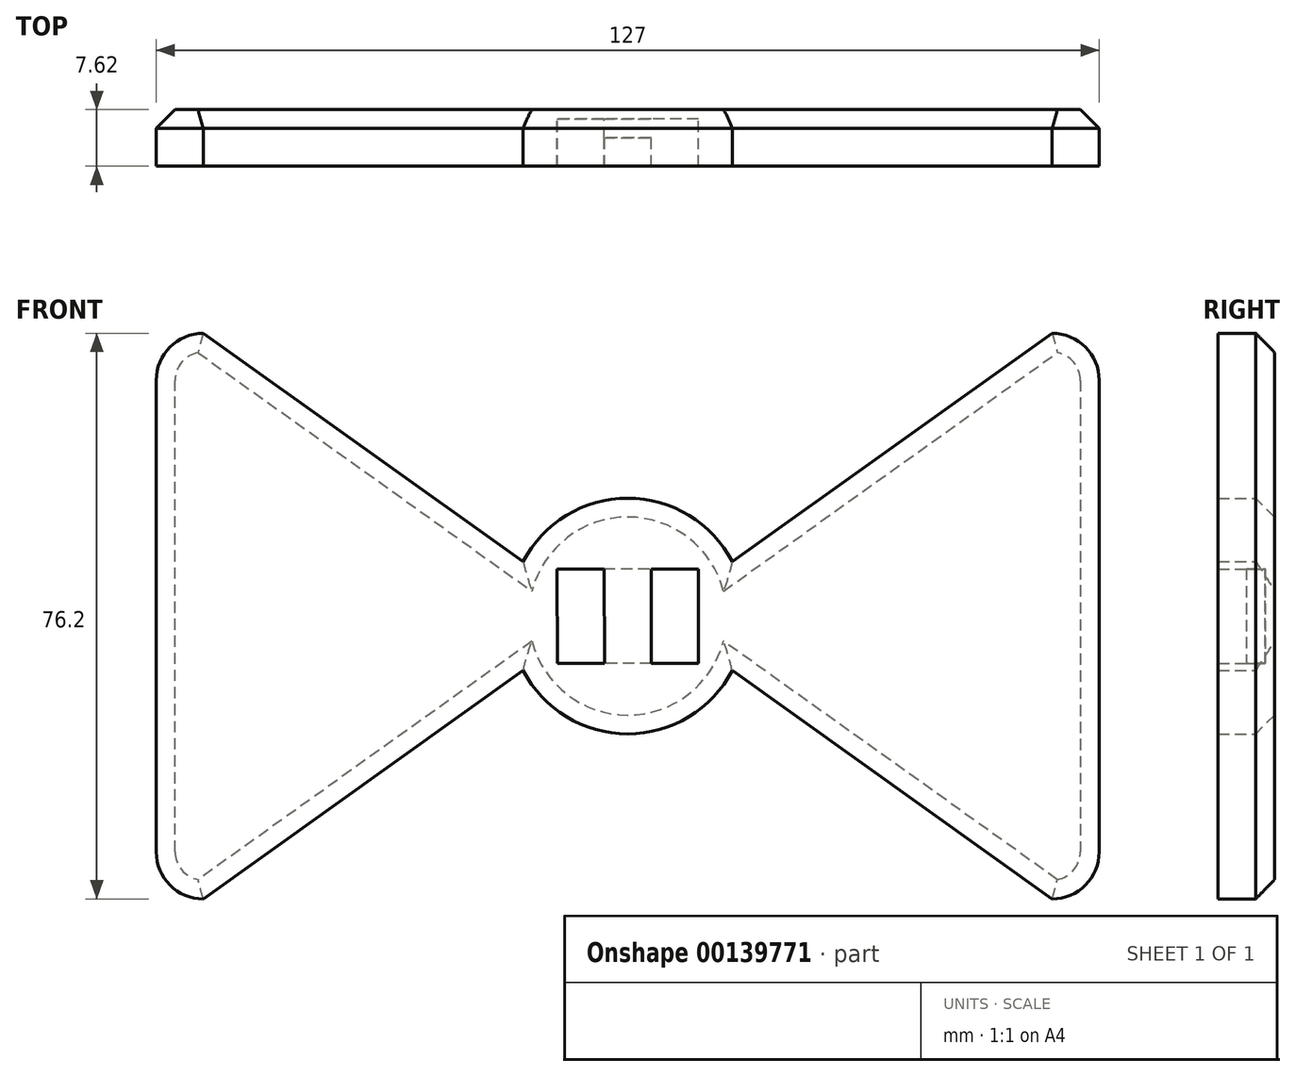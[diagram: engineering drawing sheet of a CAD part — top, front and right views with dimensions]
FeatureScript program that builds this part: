
annotation { "Feature Type Name" : "Feature", "Feature Type Description" : "" }
export const myFeature = defineFeature(function(context is Context, id is Id, definition is map)
    precondition{}
    {
        {
            var Q0;
            Q0=qCreatedBy(makeId("Front.planeOp"),FACE);
            var sketch = newSketch(context, id + "F0", { "sketchPlane" : qUnion([Q0])});
            skPoint(sketch, "E0.middle", {"position": v(0, 0) * mm});
            skPoint(sketch, "E1.endSnap0", {"position": v(12.7, 0) * mm});
            skPoint(sketch, "E2.endSnap0", {"position": v(-12.7, 0) * mm});
            skLineSegment(sketch, "E3", {"start": v(-63.5, 0) * mm, "end": v(-63.5, -31.75) * mm});
            skLineSegment(sketch, "E4", {"start": v(-63.5, 0) * mm, "end": v(-63.5, 31.75) * mm});
            skLineSegment(sketch, "E5", {"start": v(63.5, 0) * mm, "end": v(63.5, -31.75) * mm});
            skLineSegment(sketch, "E6", {"start": v(63.5, 0) * mm, "end": v(63.5, 31.75) * mm});
            skLineSegment(sketch, "E7", {"start": v(-57.15, -38.1) * mm, "end": v(-14.08, -7.33) * mm});
            skLineSegment(sketch, "E8", {"start": v(-57.15, 38.1) * mm, "end": v(-14.08, 7.33) * mm});
            skLineSegment(sketch, "E9", {"start": v(14.08, -7.33) * mm, "end": v(57.15, -38.1) * mm});
            skLineSegment(sketch, "E10", {"start": v(57.15, 38.1) * mm, "end": v(14.08, 7.33) * mm});
            skArc(sketch, "E11", {"start": v(-63.5, 31.75) * mm, "mid": v(-61.64, 36.24) * mm, "end": v(-57.15, 38.1) * mm});
            skArc(sketch, "E12", {"start": v(-63.5, -31.75) * mm, "mid": v(-61.64, -36.24) * mm, "end": v(-57.15, -38.1) * mm});
            skArc(sketch, "E13", {"start": v(63.5, 31.75) * mm, "mid": v(61.64, 36.24) * mm, "end": v(57.15, 38.1) * mm});
            skArc(sketch, "E14", {"start": v(14.08, 7.33) * mm, "mid": v(0, 15.88) * mm, "end": v(-14.08, 7.33) * mm});
            skPoint(sketch, "E15.orphan", {"position": v(-12.7, -12.7) * mm});
            skPoint(sketch, "E16.orphan", {"position": v(12.7, -12.7) * mm});
            skArc(sketch, "E17.trimOffspring", {"start": v(-14.08, -7.33) * mm, "mid": v(0, -15.88) * mm, "end": v(14.08, -7.33) * mm});
            skPoint(sketch, "E18.trimOffspring.end.orphan", {"position": v(-12.7, 12.7) * mm});
            skPoint(sketch, "E19.orphan", {"position": v(12.7, 12.7) * mm});
            skPoint(sketch, "E20.trimOffspring.start.orphan", {"position": v(12.7, 6.35) * mm});
            skArc(sketch, "E21", {"start": v(63.5, -31.75) * mm, "mid": v(61.64, -36.24) * mm, "end": v(57.15, -38.1) * mm});
            skSolve(sketch);
        }
        {
            var Q0;
            Q0=qSketchRegion(id+"F0",true);
            extrude(context, id + "F1", {"entities" : qUnion([Q0]), "depth" : 12.7 * mm});
        }
        {
            var Q0;
            Q0=qSketchRegion(id+"F0",true);
            extrude(context, id + "F2", {"entities" : qUnion([Q0]), "operationType" : NewBodyOperationType.ADD, "depth" : 12.7 * mm});
        }
        {
            var Q0;
            Q0=qCreatedBy(makeId("Front.planeOp"),FACE);
            cPlane(context, id + "F3", {"entities" : qUnion([Q0]), "cplaneType" : CPlaneType.OFFSET, "offset" : 6.35 * mm, "width" : 152.4 * mm, "height" : 152.4 * mm});
        }
        {
            var Q0;
            Q0=qCreatedBy(id+"F3.planeOp",FACE);
            var sketch = newSketch(context, id + "F4", { "sketchPlane" : qUnion([Q0])});
            skLineSegment(sketch, "E22", {"start": v(3.18, 6.35) * mm, "end": v(3.18, -6.35) * mm});
            skLineSegment(sketch, "E23", {"start": v(3.18, -6.35) * mm, "end": v(9.53, -6.35) * mm});
            skLineSegment(sketch, "E24", {"start": v(9.53, -6.35) * mm, "end": v(9.53, 6.35) * mm});
            skLineSegment(sketch, "E25", {"start": v(9.53, 6.35) * mm, "end": v(3.18, 6.35) * mm});
            skLineSegment(sketch, "E26", {"start": v(-3.17, 6.35) * mm, "end": v(-3.11, -6.35) * mm});
            skLineSegment(sketch, "E27", {"start": v(-3.17, 6.35) * mm, "end": v(-9.52, 6.32) * mm});
            skLineSegment(sketch, "E28", {"start": v(-9.52, 6.32) * mm, "end": v(-9.46, -6.38) * mm});
            skLineSegment(sketch, "E29", {"start": v(-9.46, -6.38) * mm, "end": v(-3.11, -6.35) * mm});
            skSolve(sketch);
        }
        {
            var Q0;
            Q0=qSketchRegion(id+"F4",true);
            extrude(context, id + "F5", {"entities" : qUnion([Q0]), "operationType" : NewBodyOperationType.REMOVE, "depth" : 25.4 * mm});
        }
        {
            var Q0;
            Q0=qCreatedBy(id+"F3.planeOp",FACE);
            var sketch = newSketch(context, id + "F6", { "sketchPlane" : qUnion([Q0])});
            skLineSegment(sketch, "E30", {"start": v(-3.19, 6.37) * mm, "end": v(3.18, 6.37) * mm});
            skLineSegment(sketch, "E31", {"start": v(3.18, 6.37) * mm, "end": v(3.18, -6.35) * mm});
            skLineSegment(sketch, "E32", {"start": v(3.18, -6.35) * mm, "end": v(-3.12, -6.35) * mm});
            skLineSegment(sketch, "E33", {"start": v(-3.12, -6.35) * mm, "end": v(-3.19, 6.37) * mm});
            skSolve(sketch);
        }
        {
            var Q0;
            Q0=qSketchRegion(id+"F6",true);
            extrude(context, id + "F7", {"entities" : qUnion([Q0]), "operationType" : NewBodyOperationType.REMOVE, "depth" : 2.54 * mm});
        }
        {
            var Q0;
            Q0=makeQuery(id+"F1.opExtrude","CAP_FACE",FACE,{"disambiguationData":[OSD([sQuery(id+"F0.wireOp",EDGE,"E3"),sQuery(id+"F0.wireOp",EDGE,"E4"),sQuery(id+"F0.wireOp",EDGE,"E5"),sQuery(id+"F0.wireOp",EDGE,"E6"),sQuery(id+"F0.wireOp",EDGE,"E7"),sQuery(id+"F0.wireOp",EDGE,"E8"),sQuery(id+"F0.wireOp",EDGE,"E9"),sQuery(id+"F0.wireOp",EDGE,"E10"),sQuery(id+"F0.wireOp",EDGE,"E11"),sQuery(id+"F0.wireOp",EDGE,"E12"),sQuery(id+"F0.wireOp",EDGE,"E13"),sQuery(id+"F0.wireOp",EDGE,"E14"),sQuery(id+"F0.wireOp",EDGE,"E17.trimOffspring"),sQuery(id+"F0.wireOp",EDGE,"E21")])],"isStart":true});
            var sketch = newSketch(context, id + "F8", { "sketchPlane" : qUnion([Q0])});
            skSolve(sketch);
        }
        {
            var Q0;
            Q0=makeQuery(id+"F8.imprint","IMPRINT",FACE,{"disambiguationData":[TD([[makeQuery(id+"F8.imprint","IMPRINT",EDGE,{"derivedFrom":makeQuery(id+"F1.opExtrude","CAP_EDGE",EDGE,{"disambiguationData":[OSD([sQuery(id+"F0.wireOp",EDGE,"E7")])],"isStart":true})}),-1.0]])]});
            extrude(context, id + "F9", {"entities" : qUnion([Q0]), "operationType" : NewBodyOperationType.REMOVE, "oppositeDirection" : true, "depth" : 5.08 * mm});
        }
        {
            var Q0;
            Q0=makeQuery(id+"F9.boolean.opBoolean","COPY",FACE,{"derivedFrom":makeQuery(id+"F9.opExtrude","CAP_FACE",FACE,{"disambiguationData":[OSD([sQuery(id+"F0.wireOp",EDGE,"E3"),sQuery(id+"F0.wireOp",EDGE,"E4"),sQuery(id+"F0.wireOp",EDGE,"E5"),sQuery(id+"F0.wireOp",EDGE,"E6"),sQuery(id+"F0.wireOp",EDGE,"E7"),sQuery(id+"F0.wireOp",EDGE,"E8"),sQuery(id+"F0.wireOp",EDGE,"E9"),sQuery(id+"F0.wireOp",EDGE,"E10"),sQuery(id+"F0.wireOp",EDGE,"E11"),sQuery(id+"F0.wireOp",EDGE,"E12"),sQuery(id+"F0.wireOp",EDGE,"E13"),sQuery(id+"F0.wireOp",EDGE,"E14"),sQuery(id+"F0.wireOp",EDGE,"E17.trimOffspring"),sQuery(id+"F0.wireOp",EDGE,"E21")])],"isStart":false})});
            chamfer(context, id + "F10", {"entities" : qUnion([Q0]), "width" : 2.54 * mm, "tangentPropagation" : true});
        }
    });
